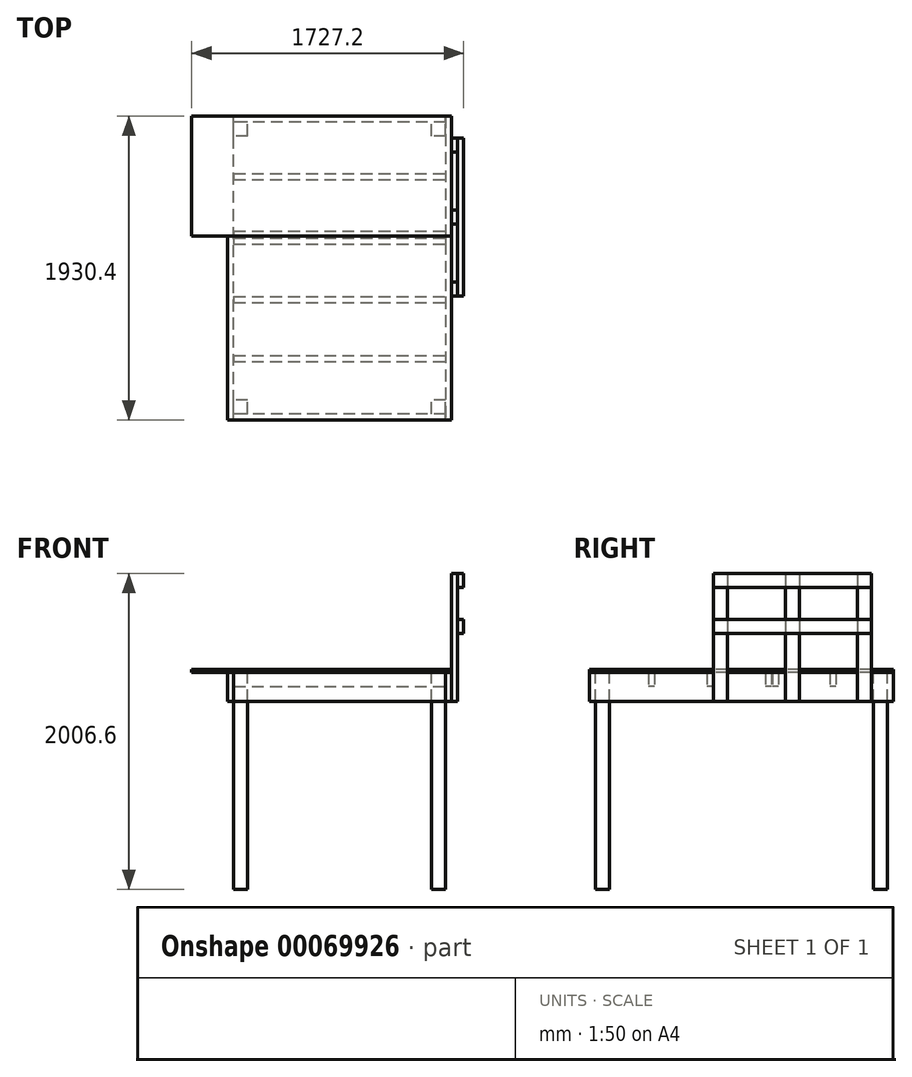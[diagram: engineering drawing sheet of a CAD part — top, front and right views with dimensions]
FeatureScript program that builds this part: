
annotation { "Feature Type Name" : "Feature", "Feature Type Description" : "" }
export const myFeature = defineFeature(function(context is Context, id is Id, definition is map)
    precondition{}
    {
        {
            var Q0;
            Q0=qCreatedBy(makeId("Front.planeOp"),FACE);
            var sketch = newSketch(context, id + "F0", { "sketchPlane" : qUnion([Q0])});
            skLineSegment(sketch, "E0.bottom", {"start": v(0, 0) * mm, "end": v(38.1, 0) * mm});
            skLineSegment(sketch, "E0.top", {"start": v(0, 184.15) * mm, "end": v(38.1, 184.15) * mm});
            skLineSegment(sketch, "E0.left", {"start": v(0, 0) * mm, "end": v(0, 184.15) * mm});
            skLineSegment(sketch, "E0.right", {"start": v(38.1, 0) * mm, "end": v(38.1, 184.15) * mm});
            skSolve(sketch);
        }
        {
            var Q0;
            Q0 = qSketchRegion(id + "F0", true);
            extrude(context, id + "F1", {"entities" : qUnion([Q0]), "depth" : 1930.4 * mm});
        }
        {
            var Q0;
            Q0=makeQuery(id+"F1.opExtrude","SWEPT_FACE",FACE,{"disambiguationData":[OSD([sQuery(id+"F0.wireOp",EDGE,"E0.right")])]});
            var sketch = newSketch(context, id + "F2", { "sketchPlane" : qUnion([Q0])});
            skLineSegment(sketch, "E1.bottom", {"start": v(-1930.4, 0) * mm, "end": v(-1892.3, 0) * mm});
            skLineSegment(sketch, "E1.top", {"start": v(-1930.4, 184.15) * mm, "end": v(-1892.3, 184.15) * mm});
            skLineSegment(sketch, "E1.left", {"start": v(-1930.4, 0) * mm, "end": v(-1930.4, 184.15) * mm});
            skLineSegment(sketch, "E1.right", {"start": v(-1892.3, 0) * mm, "end": v(-1892.3, 184.15) * mm});
            skSolve(sketch);
        }
        {
            var Q0;
            Q0 = qSketchRegion(id + "F2", true);
            extrude(context, id + "F3", {"entities" : qUnion([Q0]), "depth" : 1346.2 * mm});
        }
        {
            var Q0;
            Q0=makeQuery(id+"F3.opExtrude","SWEPT_FACE",FACE,{"disambiguationData":[OSD([sQuery(id+"F2.wireOp",EDGE,"E1.left")])]});
            var sketch = newSketch(context, id + "F4", { "sketchPlane" : qUnion([Q0])});
            skLineSegment(sketch, "E2.bottom", {"start": v(1384.3, 0) * mm, "end": v(1422.4, 0) * mm});
            skLineSegment(sketch, "E2.top", {"start": v(1384.3, 184.15) * mm, "end": v(1422.4, 184.15) * mm});
            skLineSegment(sketch, "E2.left", {"start": v(1384.3, 0) * mm, "end": v(1384.3, 184.15) * mm});
            skLineSegment(sketch, "E2.right", {"start": v(1422.4, 0) * mm, "end": v(1422.4, 184.15) * mm});
            skSolve(sketch);
        }
        {
            var Q0;
            Q0 = qSketchRegion(id + "F4", true);
            var Q1;
            Q1=makeQuery(id+"F1.opExtrude","CAP_FACE",FACE,{"disambiguationData":[OSD([sQuery(id+"F0.wireOp",EDGE,"E0.bottom"),sQuery(id+"F0.wireOp",EDGE,"E0.top"),sQuery(id+"F0.wireOp",EDGE,"E0.left"),sQuery(id+"F0.wireOp",EDGE,"E0.right")])],"isStart":true});
            extrude(context, id + "F5", {"entities" : qUnion([Q0]), "endBound" : BoundingType.UP_TO_SURFACE, "oppositeDirection" : true, "endBoundEntityFace" : qUnion([Q1]), "depth" : 25.4 * mm});
        }
        {
            var Q0;
            Q0=makeQuery(id+"F1.opExtrude","SWEPT_FACE",FACE,{"disambiguationData":[OSD([sQuery(id+"F0.wireOp",EDGE,"E0.right")])]});
            var sketch = newSketch(context, id + "F6", { "sketchPlane" : qUnion([Q0])});
            skLineSegment(sketch, "E3.bottom", {"start": v(0, 184.15) * mm, "end": v(-38.1, 184.15) * mm});
            skLineSegment(sketch, "E3.top", {"start": v(0, 0) * mm, "end": v(-38.1, 0) * mm});
            skLineSegment(sketch, "E3.left", {"start": v(0, 184.15) * mm, "end": v(0, 0) * mm});
            skLineSegment(sketch, "E3.right", {"start": v(-38.1, 184.15) * mm, "end": v(-38.1, 0) * mm});
            skSolve(sketch);
        }
        {
            var Q0;
            Q0 = qSketchRegion(id + "F6", true);
            var Q1;
            Q1=makeQuery(id+"F5.opExtrude","SWEPT_FACE",FACE,{"disambiguationData":[OSD([sQuery(id+"F4.wireOp",EDGE,"E2.left")])]});
            extrude(context, id + "F7", {"entities" : qUnion([Q0]), "endBound" : BoundingType.UP_TO_SURFACE, "endBoundEntityFace" : qUnion([Q1]), "depth" : 25.4 * mm});
        }
        {
            var Q0;
            Q0=makeQuery(id+"F5.opExtrude","SWEPT_FACE",FACE,{"disambiguationData":[OSD([sQuery(id+"F4.wireOp",EDGE,"E2.left")])]});
            var sketch = newSketch(context, id + "F8", { "sketchPlane" : qUnion([Q0])});
            skLineSegment(sketch, "E4.bottom", {"start": v(730.25, 184.15) * mm, "end": v(768.35, 184.15) * mm});
            skLineSegment(sketch, "E4.top", {"start": v(730.25, 95.25) * mm, "end": v(768.35, 95.25) * mm});
            skLineSegment(sketch, "E4.left", {"start": v(730.25, 184.15) * mm, "end": v(730.25, 95.25) * mm});
            skLineSegment(sketch, "E4.right", {"start": v(768.35, 184.15) * mm, "end": v(768.35, 95.25) * mm});
            skLineSegment(sketch, "E5.bottom", {"start": v(774.7, 184.15) * mm, "end": v(812.8, 184.15) * mm});
            skLineSegment(sketch, "E5.top", {"start": v(774.7, 95.25) * mm, "end": v(812.8, 95.25) * mm});
            skLineSegment(sketch, "E5.left", {"start": v(774.7, 184.15) * mm, "end": v(774.7, 95.25) * mm});
            skLineSegment(sketch, "E5.right", {"start": v(812.8, 184.15) * mm, "end": v(812.8, 95.25) * mm});
            skLineSegment(sketch, "E6.bottom", {"start": v(365.13, 184.15) * mm, "end": v(403.23, 184.15) * mm});
            skLineSegment(sketch, "E6.top", {"start": v(365.13, 95.25) * mm, "end": v(403.23, 95.25) * mm});
            skLineSegment(sketch, "E6.left", {"start": v(365.13, 184.15) * mm, "end": v(365.13, 95.25) * mm});
            skLineSegment(sketch, "E6.right", {"start": v(403.23, 184.15) * mm, "end": v(403.23, 95.25) * mm});
            skLineSegment(sketch, "E7.bottom", {"start": v(1147.23, 184.15) * mm, "end": v(1185.33, 184.15) * mm});
            skLineSegment(sketch, "E7.top", {"start": v(1147.23, 95.25) * mm, "end": v(1185.33, 95.25) * mm});
            skLineSegment(sketch, "E7.left", {"start": v(1147.23, 184.15) * mm, "end": v(1147.23, 95.25) * mm});
            skLineSegment(sketch, "E7.right", {"start": v(1185.33, 184.15) * mm, "end": v(1185.33, 95.25) * mm});
            skLineSegment(sketch, "E8.bottom", {"start": v(1519.77, 184.15) * mm, "end": v(1557.87, 184.15) * mm});
            skLineSegment(sketch, "E8.top", {"start": v(1519.77, 95.25) * mm, "end": v(1557.87, 95.25) * mm});
            skLineSegment(sketch, "E8.left", {"start": v(1519.77, 184.15) * mm, "end": v(1519.77, 95.25) * mm});
            skLineSegment(sketch, "E8.right", {"start": v(1557.87, 184.15) * mm, "end": v(1557.87, 95.25) * mm});
            skLineSegment(sketch, "E9", {"start": v(812.8, 139.7) * mm, "end": v(1147.23, 139.7) * mm, "construction": true});
            skLineSegment(sketch, "E10", {"start": v(1185.33, 139.7) * mm, "end": v(1519.77, 139.7) * mm, "construction": true});
            skLineSegment(sketch, "E11", {"start": v(1557.87, 139.7) * mm, "end": v(1892.3, 139.7) * mm, "construction": true});
            skLineSegment(sketch, "E12", {"start": v(38.1, 139.7) * mm, "end": v(365.13, 139.7) * mm, "construction": true});
            skPoint(sketch, "E12.startSnap0", {"position": v(-91.48, 139.7) * mm});
            skLineSegment(sketch, "E13", {"start": v(403.23, 139.7) * mm, "end": v(730.25, 139.7) * mm, "construction": true});
            skPoint(sketch, "E14", {"position": v(730.25, 139.7) * mm});
            skSolve(sketch);
        }
        {
            var Q0;
            Q0 = qSketchRegion(id + "F8", true);
            var Q1;
            Q1=makeQuery(id+"F1.opExtrude","SWEPT_FACE",FACE,{"disambiguationData":[OSD([sQuery(id+"F0.wireOp",EDGE,"E0.right")])]});
            extrude(context, id + "F9", {"entities" : qUnion([Q0]), "endBound" : BoundingType.UP_TO_SURFACE, "endBoundEntityFace" : qUnion([Q1]), "depth" : 25.4 * mm});
        }
        {
            var Q0;
            Q0=makeQuery(id+"F5.opExtrude","SWEPT_FACE",FACE,{"disambiguationData":[OSD([sQuery(id+"F4.wireOp",EDGE,"E2.top")])]});
            var sketch = newSketch(context, id + "F10", { "sketchPlane" : qUnion([Q0])});
            skLineSegment(sketch, "E15.bottom", {"start": v(1422.4, 0) * mm, "end": v(-228.6, 0) * mm});
            skLineSegment(sketch, "E15.top", {"start": v(1422.4, -762) * mm, "end": v(-228.6, -762) * mm});
            skLineSegment(sketch, "E15.left", {"start": v(1422.4, 0) * mm, "end": v(1422.4, -762) * mm});
            skLineSegment(sketch, "E15.right", {"start": v(-228.6, 0) * mm, "end": v(-228.6, -762) * mm});
            skSolve(sketch);
        }
        {
            var Q0;
            Q0 = qSketchRegion(id + "F10", true);
            extrude(context, id + "F11", {"entities" : qUnion([Q0]), "depth" : 19.05 * mm});
        }
        {
            var Q0;
            Q0=makeQuery(id+"F5.opExtrude","SWEPT_FACE",FACE,{"disambiguationData":[OSD([sQuery(id+"F4.wireOp",EDGE,"E2.top")])]});
            var sketch = newSketch(context, id + "F12", { "sketchPlane" : qUnion([Q0])});
            skLineSegment(sketch, "E16.bottom", {"start": v(1422.4, -1930.4) * mm, "end": v(0, -1930.4) * mm});
            skLineSegment(sketch, "E16.top", {"start": v(1422.4, -762) * mm, "end": v(0, -762) * mm});
            skLineSegment(sketch, "E16.left", {"start": v(1422.4, -1930.4) * mm, "end": v(1422.4, -762) * mm});
            skLineSegment(sketch, "E16.right", {"start": v(0, -1930.4) * mm, "end": v(0, -762) * mm});
            skSolve(sketch);
        }
        {
            var Q0;
            Q0 = qSketchRegion(id + "F12", true);
            var Q1;
            Q1=makeQuery(id+"F11.opExtrude","CAP_FACE",FACE,{"disambiguationData":[OSD([sQuery(id+"F10.wireOp",EDGE,"E15.bottom"),sQuery(id+"F10.wireOp",EDGE,"E15.top"),sQuery(id+"F10.wireOp",EDGE,"E15.left"),sQuery(id+"F10.wireOp",EDGE,"E15.right")])],"isStart":false});
            extrude(context, id + "F13", {"entities" : qUnion([Q0]), "endBound" : BoundingType.UP_TO_SURFACE, "endBoundEntityFace" : qUnion([Q1]), "depth" : 25.4 * mm});
        }
        {
            var Q0;
            Q0=makeQuery(id+"F13.opExtrude","CAP_FACE",FACE,{"disambiguationData":[OSD([sQuery(id+"F12.wireOp",EDGE,"E16.bottom"),sQuery(id+"F12.wireOp",EDGE,"E16.top"),sQuery(id+"F12.wireOp",EDGE,"E16.left"),sQuery(id+"F12.wireOp",EDGE,"E16.right")])],"isStart":true});
            var sketch = newSketch(context, id + "F14", { "sketchPlane" : qUnion([Q0])});
            skLineSegment(sketch, "E17.bottom", {"start": v(1384.3, 1892.3) * mm, "end": v(1295.4, 1892.3) * mm});
            skLineSegment(sketch, "E17.top", {"start": v(1384.3, 1803.4) * mm, "end": v(1295.4, 1803.4) * mm});
            skLineSegment(sketch, "E17.left", {"start": v(1384.3, 1892.3) * mm, "end": v(1384.3, 1803.4) * mm});
            skLineSegment(sketch, "E17.right", {"start": v(1295.4, 1892.3) * mm, "end": v(1295.4, 1803.4) * mm});
            skLineSegment(sketch, "E18.bottom", {"start": v(127, 1892.3) * mm, "end": v(38.1, 1892.3) * mm});
            skLineSegment(sketch, "E18.top", {"start": v(127, 1803.4) * mm, "end": v(38.1, 1803.4) * mm});
            skLineSegment(sketch, "E18.left", {"start": v(127, 1892.3) * mm, "end": v(127, 1803.4) * mm});
            skLineSegment(sketch, "E18.right", {"start": v(38.1, 1892.3) * mm, "end": v(38.1, 1803.4) * mm});
            skLineSegment(sketch, "E19.bottom", {"start": v(127, 127) * mm, "end": v(38.1, 127) * mm});
            skLineSegment(sketch, "E19.top", {"start": v(127, 38.1) * mm, "end": v(38.1, 38.1) * mm});
            skLineSegment(sketch, "E19.left", {"start": v(127, 127) * mm, "end": v(127, 38.1) * mm});
            skLineSegment(sketch, "E19.right", {"start": v(38.1, 127) * mm, "end": v(38.1, 38.1) * mm});
            skLineSegment(sketch, "E20.bottom", {"start": v(1384.3, 127) * mm, "end": v(1295.4, 127) * mm});
            skLineSegment(sketch, "E20.top", {"start": v(1384.3, 38.1) * mm, "end": v(1295.4, 38.1) * mm});
            skLineSegment(sketch, "E20.left", {"start": v(1384.3, 127) * mm, "end": v(1384.3, 38.1) * mm});
            skLineSegment(sketch, "E20.right", {"start": v(1295.4, 127) * mm, "end": v(1295.4, 38.1) * mm});
            skSolve(sketch);
        }
        {
            var Q0;
            Q0 = qSketchRegion(id + "F14", true);
            extrude(context, id + "F15", {"entities" : qUnion([Q0]), "depth" : 1377.95 * mm});
        }
        {
            var Q0;
            Q0=makeQuery(id+"F5.opExtrude","SWEPT_FACE",FACE,{"disambiguationData":[OSD([sQuery(id+"F4.wireOp",EDGE,"E2.bottom")])]});
            var sketch = newSketch(context, id + "F16", { "sketchPlane" : qUnion([Q0])});
            skLineSegment(sketch, "E21.bottom", {"start": v(1422.4, 1143) * mm, "end": v(1460.5, 1143) * mm});
            skLineSegment(sketch, "E21.top", {"start": v(1422.4, 1054.1) * mm, "end": v(1460.5, 1054.1) * mm});
            skLineSegment(sketch, "E21.left", {"start": v(1422.4, 1143) * mm, "end": v(1422.4, 1054.1) * mm});
            skLineSegment(sketch, "E21.right", {"start": v(1460.5, 1143) * mm, "end": v(1460.5, 1054.1) * mm});
            skLineSegment(sketch, "E22.bottom", {"start": v(1422.4, 228.6) * mm, "end": v(1460.5, 228.6) * mm});
            skLineSegment(sketch, "E22.top", {"start": v(1422.4, 139.7) * mm, "end": v(1460.5, 139.7) * mm});
            skLineSegment(sketch, "E22.left", {"start": v(1422.4, 228.6) * mm, "end": v(1422.4, 139.7) * mm});
            skLineSegment(sketch, "E22.right", {"start": v(1460.5, 228.6) * mm, "end": v(1460.5, 139.7) * mm});
            skLineSegment(sketch, "E23.bottom", {"start": v(1422.4, 685.8) * mm, "end": v(1460.5, 685.8) * mm});
            skLineSegment(sketch, "E23.top", {"start": v(1422.4, 596.9) * mm, "end": v(1460.5, 596.9) * mm});
            skLineSegment(sketch, "E23.left", {"start": v(1422.4, 685.8) * mm, "end": v(1422.4, 596.9) * mm});
            skLineSegment(sketch, "E23.right", {"start": v(1460.5, 685.8) * mm, "end": v(1460.5, 596.9) * mm});
            skLineSegment(sketch, "E24", {"start": v(1460.5, 1054.1) * mm, "end": v(1460.5, 685.8) * mm, "construction": true});
            skLineSegment(sketch, "E25", {"start": v(1460.5, 596.9) * mm, "end": v(1460.5, 228.6) * mm, "construction": true});
            skSolve(sketch);
        }
        {
            var Q0;
            Q0 = qSketchRegion(id + "F16", true);
            extrude(context, id + "F17", {"entities" : qUnion([Q0]), "oppositeDirection" : true, "depth" : 812.8 * mm, "offsetDistance" : 25.4 * mm});
        }
        {
            var Q0;
            Q0=makeQuery(id+"F17.opExtrude","SWEPT_FACE",FACE,{"disambiguationData":[OSD([sQuery(id+"F16.wireOp",EDGE,"E21.bottom")])]});
            var sketch = newSketch(context, id + "F18", { "sketchPlane" : qUnion([Q0])});
            skLineSegment(sketch, "E26.bottom", {"start": v(1460.5, 812.8) * mm, "end": v(1498.6, 812.8) * mm});
            skLineSegment(sketch, "E26.top", {"start": v(1460.5, 723.9) * mm, "end": v(1498.6, 723.9) * mm});
            skLineSegment(sketch, "E26.left", {"start": v(1460.5, 812.8) * mm, "end": v(1460.5, 723.9) * mm});
            skLineSegment(sketch, "E26.right", {"start": v(1498.6, 812.8) * mm, "end": v(1498.6, 723.9) * mm});
            skLineSegment(sketch, "E27.bottom", {"start": v(1460.5, 520.7) * mm, "end": v(1498.6, 520.7) * mm});
            skLineSegment(sketch, "E27.top", {"start": v(1460.5, 431.8) * mm, "end": v(1498.6, 431.8) * mm});
            skLineSegment(sketch, "E27.left", {"start": v(1460.5, 520.7) * mm, "end": v(1460.5, 431.8) * mm});
            skLineSegment(sketch, "E27.right", {"start": v(1498.6, 520.7) * mm, "end": v(1498.6, 431.8) * mm});
            skSolve(sketch);
        }
        {
            var Q0;
            Q0 = qSketchRegion(id + "F18", true);
            var Q1;
            Q1=makeQuery(id+"F17.opExtrude","SWEPT_FACE",FACE,{"disambiguationData":[OSD([sQuery(id+"F16.wireOp",EDGE,"E22.top")])]});
            extrude(context, id + "F19", {"entities" : qUnion([Q0]), "endBound" : BoundingType.UP_TO_SURFACE, "oppositeDirection" : true, "depth" : 25.4 * mm, "endBoundEntityFace" : qUnion([Q1]), "offsetDistance" : 25.4 * mm});
        }
    });
